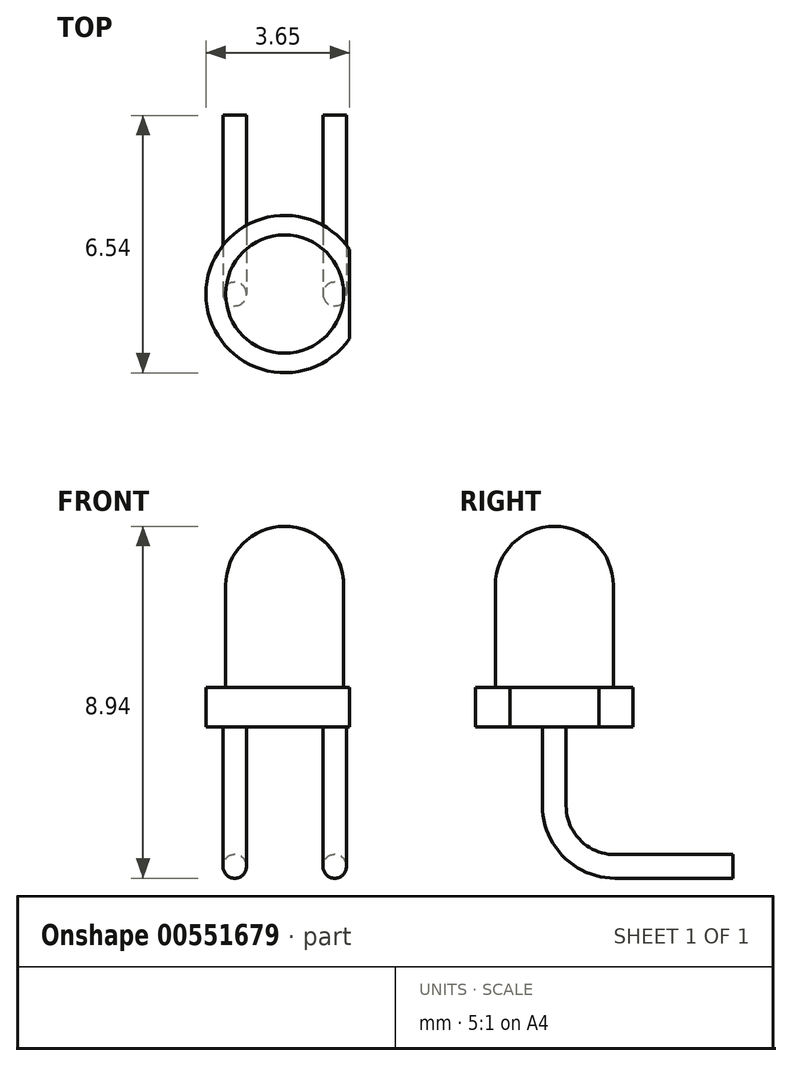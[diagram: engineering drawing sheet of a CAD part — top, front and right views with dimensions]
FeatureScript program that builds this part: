
annotation { "Feature Type Name" : "Feature", "Feature Type Description" : "" }
export const myFeature = defineFeature(function(context is Context, id is Id, definition is map)
    precondition{}
    {
        {
            var Q0;
            Q0=qCreatedBy(makeId("Front.planeOp"),FACE);
            var sketch = newSketch(context, id + "F0", { "sketchPlane" : qUnion([Q0])});
            skLineSegment(sketch, "E0", {"start": v(0, 0) * mm, "end": v(0, 3.6) * mm});
            skLineSegment(sketch, "E1", {"start": v(1.5, 3.6) * mm, "end": v(1.5, 1) * mm});
            skLineSegment(sketch, "E2", {"start": v(1.5, 0) * mm, "end": v(0, 0) * mm});
            skLineSegment(sketch, "E3", {"start": v(1.5, 0) * mm, "end": v(2, 0) * mm});
            skLineSegment(sketch, "E4", {"start": v(2, 0) * mm, "end": v(2, 1) * mm});
            skLineSegment(sketch, "E5", {"start": v(2, 1) * mm, "end": v(1.5, 1) * mm});
            skArc(sketch, "E6", {"start": v(1.5, 3.6) * mm, "mid": v(1.06, 4.66) * mm, "end": v(0, 5.1) * mm});
            skLineSegment(sketch, "E7", {"start": v(0, 5.1) * mm, "end": v(0, 3.6) * mm});
            skSolve(sketch);
        }
        {
            var Q0;
            Q0 = qSketchRegion(id + "F0", true);
            var Q1;
            Q1=sQuery(id+"F0.wireOp",EDGE,"E0");
            revolve(context, id + "F1", {"entities" : qUnion([Q0]), "axis" : qUnion([Q1]), "revolveType" : RevolveType.FULL});
        }
        {
            var Q0;
            Q0=qCreatedBy(makeId("Top.planeOp"),FACE);
            var sketch = newSketch(context, id + "F2", { "sketchPlane" : qUnion([Q0])});
            skCircle(sketch, "E8", {"center": v(-1.27, 0) * mm, "radius": 0.3 * mm});
            skCircle(sketch, "E9", {"center": v(1.27, 0) * mm, "radius": 0.3 * mm});
            skLineSegment(sketch, "E10", {"start": v(1.65, 0) * mm, "end": v(1.65, -1.2) * mm});
            skLineSegment(sketch, "E11", {"start": v(1.65, 0) * mm, "end": v(1.65, 1.42) * mm});
            skCircle(sketch, "E12.0", {"center": v(0, 0) * mm, "radius": 2 * mm});
            skSolve(sketch);
        }
        {
            var Q0;
            Q0=makeQuery(id+"F2.imprint","IMPRINT",FACE,{"disambiguationData":[TD([[makeQuery(id+"F2.imprint","IMPRINT",EDGE,{"derivedFrom":sQuery(id+"F2.wireOp",EDGE,"E8")}),1.0]])]});
            var Q1;
            Q1=makeQuery(id+"F2.imprint","IMPRINT",FACE,{"disambiguationData":[TD([[makeQuery(id+"F2.imprint","IMPRINT",EDGE,{"derivedFrom":sQuery(id+"F2.wireOp",EDGE,"E9")}),1.0]])]});
            extrude(context, id + "F3", {"entities" : qUnion([Q0, Q1]), "operationType" : NewBodyOperationType.ADD, "oppositeDirection" : true, "depth" : 2 * mm, "offsetDistance" : 25 * mm});
        }
        {
            var Q0;
            {var subQ0=sQuery(id+"F2.wireOp",EDGE,"E11");var subQ1=sQuery(id+"F2.wireOp",EDGE,"E10");var subQ2=makeQuery(id+"F2.imprint","INTERSECT",VERTEX,{"derivedFrom":[subQ1,subQ0]});Q0=makeQuery(id+"F2.imprint","IMPRINT",FACE,{"disambiguationData":[TD([[makeQuery(id+"F2.imprint","IMPRINT",EDGE,{"disambiguationData":[TD([[subQ2,-1.0]])],"derivedFrom":subQ1}),1.0]])]});}
            extrude(context, id + "F4", {"entities" : qUnion([Q0]), "operationType" : NewBodyOperationType.REMOVE, "depth" : 25 * mm, "offsetDistance" : 25 * mm});
        }
        {
            var Q0;
            Q0=makeQuery(id+"F3.opExtrude","CAP_FACE",FACE,{"disambiguationData":[OSD([sQuery(id+"F2.wireOp",EDGE,"E8")])],"isStart":false});
            var sketch = newSketch(context, id + "F5", { "sketchPlane" : qUnion([Q0])});
            skCircle(sketch, "E13.0", {"center": v(-1.27, 0) * mm, "radius": 0.3 * mm});
            skCircle(sketch, "E13.1", {"center": v(1.27, 0) * mm, "radius": 0.3 * mm});
            skLineSegment(sketch, "E14", {"start": v(-1.8, -1.54) * mm, "end": v(1.92, -1.54) * mm, "construction": true});
            skSolve(sketch);
        }
        {
            var Q0;
            Q0=makeQuery(id+"F5.imprint","IMPRINT",FACE,{"disambiguationData":[TD([[makeQuery(id+"F5.imprint","IMPRINT",EDGE,{"derivedFrom":sQuery(id+"F5.wireOp",EDGE,"E13.0")}),-1.0]])]});
            var Q1;
            Q1=makeQuery(id+"F5.imprint","IMPRINT",FACE,{"disambiguationData":[TD([[makeQuery(id+"F5.imprint","IMPRINT",EDGE,{"derivedFrom":sQuery(id+"F5.wireOp",EDGE,"E13.1")}),1.0]])]});
            var Q2;
            Q2 = qSketchRegion(id + "F7", true);
            var Q3;
            Q3=sQuery(id+"F5.wireOp",EDGE,"E14");
            var Q4;
            Q4=sQuery(id+"F5.wireOp",EDGE,"E14");
            revolve(context, id + "F6", {"operationType" : NewBodyOperationType.ADD, "entities" : qUnion([Q0, Q1, Q2]), "surfaceEntities" : qUnion([Q3]), "axis" : qUnion([Q4]), "revolveType" : RevolveType.ONE_DIRECTION, "angle" : 90 * degree});
        }
        {
            var Q0;
            Q0=makeQuery(id+"F6.opRevolve","CAP_FACE",FACE,{"disambiguationData":[OSD([sQuery(id+"F5.wireOp",EDGE,"E13.1")])],"isStart":false});
            var sketch = newSketch(context, id + "F7", { "sketchPlane" : qUnion([Q0])});
            skCircle(sketch, "E15.0", {"center": v(-1.27, -3.54) * mm, "radius": 0.3 * mm});
            skSolve(sketch);
        }
        {
            var Q0;
            Q0=makeQuery(id+"F6.opRevolve","CAP_FACE",FACE,{"disambiguationData":[OSD([sQuery(id+"F5.wireOp",EDGE,"E13.0")])],"isStart":false});
            var Q1;
            Q1=makeQuery(id+"F7.imprint","IMPRINT",FACE,{"disambiguationData":[TD([[makeQuery(id+"F7.imprint","IMPRINT",EDGE,{"derivedFrom":sQuery(id+"F7.wireOp",EDGE,"E15.0")}),1.0]])]});
            extrude(context, id + "F8", {"entities" : qUnion([Q0, Q1]), "operationType" : NewBodyOperationType.ADD, "depth" : 3 * mm, "offsetDistance" : 25 * mm});
        }
    });
